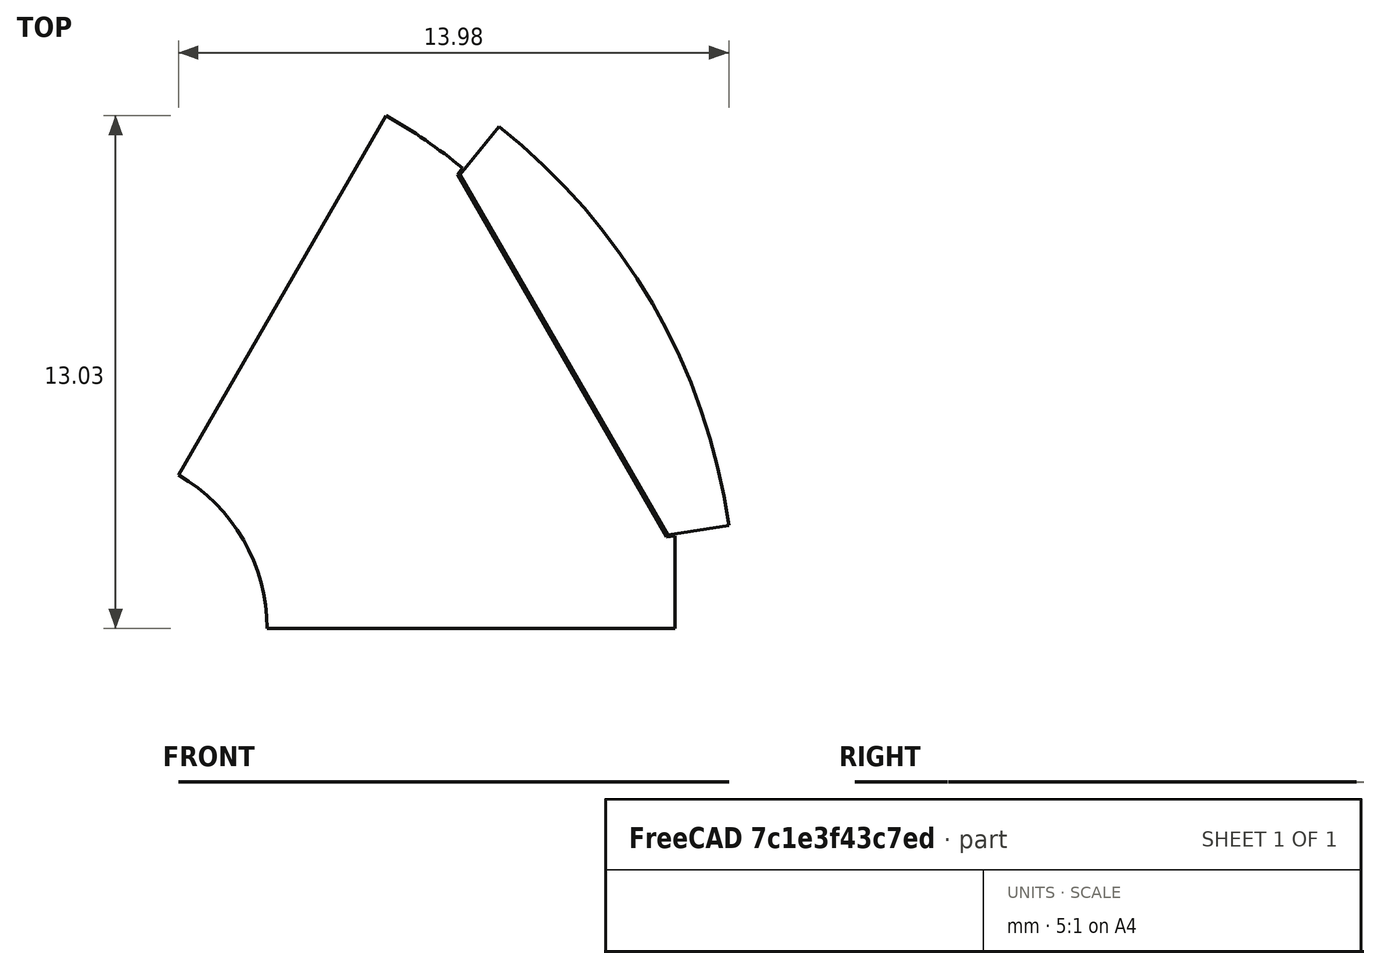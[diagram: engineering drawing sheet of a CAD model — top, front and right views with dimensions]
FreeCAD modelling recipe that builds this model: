
FCSTD DOCUMENT  (FreeCAD 0.18R4 (GitTag))
Label: rotor4
License: All rights reserved
LicenseURL: http://en.wikipedia.org/wiki/All_rights_reserved
objects: Sketcher::SketchObject×5, PartDesign::Body×2, Surface::Filling×2, Spreadsheet::Sheet×1
note: 9 computed .brp shape members not serialized (recipe doc carries the construction recipe); baked Part::Feature solids carry a one-line shape summary decoded from their .brp

FEATURE [Spreadsheet::Sheet] Spreadsheet  label="Variables"
  cells = A2=poleNumber; B2(poleNumber)=6; A3=outerDiameter; B3(outerDiameter)=33; D3=Calc Value; A4=innerDiameter; B4(innerDiameter)=9; D4=Input Value; A5=stackLength; B5(stackLength)=20; A6=stackingFactor; B6(stackingFactor)=0.95; A7=embrace; B7(embrace)=75; A8=contourRatio; B8(contourRatio)=80; A9=magnetAirgap; B9(magnetAirgap)=0.05; A10=poleSeparation; B10(poleSeparation)=2; A11=magnetWidth; B11(magnetWidth)=9; A12=magnetHeight; B12(magnetHeight)=2.8; A13=rib; B13(rib)=0.5; A14=bridgeCurved; B14(bridgeCurved)=0.5; A15=cutTop; B15(cutTop)=0.2; A16=cutBottom; B16(cutBottom)=0.25; A17=segmentAngle; B17(segmentAngle)==360 / poleNumber; A18=movePocketInwards; B18(movePocketInwards)=0.5; A19=cuttingThickness; B19(cuttingThickness)=0.1; A20=magnetLength; B20(magnetLength)==stackLength; A21=cut; B21(cut)=0.2; A22=ribShaft; B22(ribShaft)=0.5; A23=magnetEmbrace; B23(magnetEmbrace)=70; A24=magnetContourRatio; B24(magnetContourRatio)=95; A25=axialMisalignment; B25(axialMisalignment)=0.5
FEATURE [Sketcher::SketchObject] Sketch003  label="RotorSketch"
  MapMode = 5
  Support = -> [XY_Plane]
  expr: Constraints[32] = Variables.outerDiameter / 2 - Variables.magnetHeight - Variables.magnetAirgap + Spreadsheet.cutTop
  expr: Constraints[28] = Variables.segmentAngle * Variables.magnetEmbrace / 100
  expr: Constraints[15] = Variables.outerDiameter / 2
  expr: Constraints[14] = Variables.innerDiameter / 2
  expr: Constraints[50] = Spreadsheet.cut
  expr: Constraints[18] = Variables.segmentAngle / 2
  expr: Constraints[0] = Variables.segmentAngle
  expr: Constraints[23] = Variables.outerDiameter / 2 * Variables.magnetContourRatio / 100
  sketch-geometry (22):
    g0: LineSegment [constr] StartX=4.5 StartY=0 StartZ=0 EndX=16.5 EndY=0 EndZ=0
    g1: LineSegment [constr] StartX=2.25 StartY=3.89711 StartZ=0 EndX=8.25 EndY=14.2894 EndZ=0
    g2: LineSegment [constr] StartX=0 StartY=0 StartZ=0 EndX=4.5 EndY=0 EndZ=0
    g3: LineSegment [constr] StartX=0 StartY=0 StartZ=0 EndX=2.25 EndY=3.89711 EndZ=0
    g4: ArcOfCircle [constr] CenterX=0 CenterY=0 CenterZ=0 NormalX=0 NormalY=0 NormalZ=1 AngleXU=0 Radius=16.5 StartAngle=0 EndAngle=1.0472
    g5: ArcOfCircle CenterX=0 CenterY=0 CenterZ=0 NormalX=0 NormalY=0 NormalZ=1 AngleXU=0 Radius=4.5 StartAngle=0 EndAngle=1.0472
    g6: LineSegment [constr] StartX=0 StartY=0 StartZ=0 EndX=14.2894 EndY=8.25 EndZ=0
    g7: ArcOfCircle [constr] CenterX=0.714471 CenterY=0.4125 CenterZ=0 NormalX=0 NormalY=0 NormalZ=1 AngleXU=0 Radius=15.675 StartAngle=6.25687 EndAngle=7.3567
    g8: LineSegment [constr] StartX=0 StartY=0 StartZ=0 EndX=10.3838 EndY=12.8229 EndZ=0
    g9: LineSegment [constr] StartX=0 StartY=0 StartZ=0 EndX=16.2969 EndY=2.58117 EndZ=0
    g10: ArcOfCircle [constr] CenterX=0 CenterY=0 CenterZ=0 NormalX=0 NormalY=0 NormalZ=1 AngleXU=0 Radius=13.85 StartAngle=0 EndAngle=1.0472
    g11: LineSegment [constr] StartX=0 StartY=0 StartZ=0 EndX=9.33619 EndY=11.5292 EndZ=0
    g12: LineSegment [constr] StartX=0 StartY=0 StartZ=0 EndX=14.6527 EndY=2.32076 EndZ=0
    g13: LineSegment StartX=9.33619 StartY=11.5292 StartZ=0 EndX=14.6527 EndY=2.32076 EndZ=0
    g14: ArcOfCircle CenterX=0 CenterY=0 CenterZ=0 NormalX=0 NormalY=0 NormalZ=1 AngleXU=0 Radius=15.0496 StartAngle=0.890118 EndAngle=1.0472
    g15: LineSegment StartX=9.47101 StartY=11.6957 StartZ=0 EndX=9.33619 EndY=11.5292 EndZ=0
    g16: LineSegment [constr] StartX=9.33619 StartY=11.5292 StartZ=0 EndX=9.5094 EndY=11.6292 EndZ=0
    g17: LineSegment [constr] StartX=9.5094 StartY=11.6292 StartZ=0 EndX=9.47101 EndY=11.6957 EndZ=0
    g18: LineSegment StartX=14.6527 StartY=2.32076 StartZ=0 EndX=14.8643 EndY=2.35427 EndZ=0
    g19: LineSegment StartX=14.8643 StartY=2.35427 StartZ=0 EndX=14.8643 EndY=0 EndZ=0
    g20: LineSegment StartX=2.25 StartY=3.89711 StartZ=0 EndX=7.52479 EndY=13.0333 EndZ=0
    g21: LineSegment StartX=4.5 StartY=0 StartZ=0 EndX=14.8643 EndY=0 EndZ=0
  constraints (62):
    c: Angle(g0,g1) = 1.0472
    c: Coincident(g2,g-1)
    c: Coincident(g2,g0)
    c: Coincident(g3,g2)
    c: Coincident(g3,g1)
    c: Parallel(g2,g0)
    c: Parallel(g3,g1)
    c: Coincident(g4,g-1)
    c: Coincident(g4,g0)
    c: Coincident(g4,g1)
    c: Coincident(g5,g4)
    c: Coincident(g5,g1)
    c: Coincident(g5,g0)
    c: Angle(g-1,g2) = 0
    c: Radius(g5) = 4.5
    c: Radius(g4) = 16.5
    c: Coincident(g6,g5)
    c: PointOnObject(g6,g4)
    c: Angle(g-1,g6) = 0.523599
    c: PointOnObject(g7,g1)
    c: PointOnObject(g7,g0)
    c: PointOnObject(g6,g7)
    c: PointOnObject(g7,g6)
    c: Radius(g7) = 15.675
    c: Coincident(g8,g5)
    c: PointOnObject(g8,g4)
    c: Coincident(g9,g5)
    c: Symmetric(g8,g9,g6)
    c: Angle(g9,g8) = 0.733038
    c: Coincident(g10,g5)
    c: PointOnObject(g10,g1)
    c: PointOnObject(g10,g0)
    c: Radius(g10) = 13.85
    c: Coincident(g11,g5)
    c: PointOnObject(g11,g8)
    c: Coincident(g12,g5)
    c: PointOnObject(g12,g9)
    c: Equal(g11,g12)
    c: Coincident(g13,g11)
    c: Coincident(g13,g12)
    c: Tangent(g13,g10)
    c: Coincident(g14,g5)
    c: PointOnObject(g14,g8)
    c: Coincident(g15,g14)
    c: Coincident(g15,g13)
    c: Coincident(g16,g13)
    c: Coincident(g17,g16)
    c: Coincident(g17,g14)
    c: Angle(g17,g16) = 1.5708
    c: Angle(g13,g16) = 1.5708
    c: Distance(g16) = 0.2
    c: PointOnObject(g14,g1)
    c: Coincident(g18,g13)
    c: PointOnObject(g18,g9)
    c: Coincident(g19,g18)
    c: PointOnObject(g19,g0)
    c: Vertical(g19)
    c: Equal(g18,g15)
    c: Coincident(g20,g5)
    c: Coincident(g20,g14)
    c: Coincident(g21,g5)
    c: Coincident(g21,g19)
FEATURE [Sketcher::SketchObject] Sketch004  label="BoundingBox"
  MapMode = 5
  Support = -> [XY_Plane]
  expr: Constraints[8] = Variables.outerDiameter
  sketch-geometry (6):
    g0: LineSegment StartX=-16.5 StartY=-16.5 StartZ=0 EndX=16.5 EndY=-16.5 EndZ=0
    g1: LineSegment StartX=16.5 StartY=-16.5 StartZ=0 EndX=16.5 EndY=16.5 EndZ=0
    g2: LineSegment StartX=16.5 StartY=16.5 StartZ=0 EndX=-16.5 EndY=16.5 EndZ=0
    g3: LineSegment StartX=-16.5 StartY=16.5 StartZ=0 EndX=-16.5 EndY=-16.5 EndZ=0
    g4: LineSegment [constr] StartX=-16.5 StartY=-16.5 StartZ=0 EndX=16.5 EndY=16.5 EndZ=0
    g5: GeomPoint X=0 Y=0 Z=0
  constraints (14):
    c: Coincident(g0,g1)
    c: Coincident(g1,g2)
    c: Coincident(g2,g3)
    c: Coincident(g3,g0)
    c: Horizontal(g0)
    c: Horizontal(g2)
    c: Vertical(g1)
    c: Vertical(g3)
    c: DistanceY(g1,g1) = 33
    c: Equal(g2,g1)
    c: Coincident(g4,g0)
    c: Coincident(g4,g1)
    c: Symmetric(g0,g1,g5)
    c: Coincident(g-1,g5)
FEATURE [Sketcher::SketchObject] Sketch005  label="RotorSideSketch"
  MapMode = 5
  Support = -> [XY_Plane001]
  expr: Constraints[22] = Variables.stackLength / 2 - Variables.axialMisalignment
  expr: Constraints[9] = Variables.outerDiameter / 2
  expr: Constraints[8] = Variables.innerDiameter / 2
  expr: Constraints[7] = Variables.stackLength
  sketch-geometry (8):
    g0: LineSegment StartX=-9.5 StartY=4.5 StartZ=0 EndX=10.5 EndY=4.5 EndZ=0
    g1: LineSegment StartX=10.5 StartY=4.5 StartZ=0 EndX=10.5 EndY=16.5 EndZ=0
    g2: LineSegment StartX=10.5 StartY=16.5 StartZ=0 EndX=-9.5 EndY=16.5 EndZ=0
    g3: LineSegment StartX=-9.5 StartY=16.5 StartZ=0 EndX=-9.5 EndY=4.5 EndZ=0
    g4: LineSegment StartX=-9.5 StartY=-4.5 StartZ=0 EndX=10.5 EndY=-4.5 EndZ=0
    g5: LineSegment StartX=10.5 StartY=-4.5 StartZ=0 EndX=10.5 EndY=-16.5 EndZ=0
    g6: LineSegment StartX=10.5 StartY=-16.5 StartZ=0 EndX=-9.5 EndY=-16.5 EndZ=0
    g7: LineSegment StartX=-9.5 StartY=-16.5 StartZ=0 EndX=-9.5 EndY=-4.5 EndZ=0
  constraints (23):
    c: Coincident(g0,g1)
    c: Coincident(g1,g2)
    c: Coincident(g2,g3)
    c: Coincident(g3,g0)
    c: Horizontal(g0)
    c: Vertical(g1)
    c: Vertical(g3)
    c: DistanceX(g2,g2) = 20
    c: DistanceY(g-1,g0) = 4.5
    c: DistanceY(g-1,g1) = 16.5
    c: Coincident(g4,g5)
    c: Coincident(g5,g6)
    c: Coincident(g6,g7)
    c: Coincident(g7,g4)
    c: Horizontal(g4)
    c: Vertical(g5)
    c: Vertical(g7)
    c: Equal(g4,g0)
    c: Equal(g7,g3)
    c: Horizontal(g6)
    c: Horizontal(g2)
    c: Symmetric(g0,g4,g-1)
    c: DistanceX(g0,g-1) = 9.5
FEATURE [Sketcher::SketchObject] Sketch006  label="MagnetSideSketch"
  ExternalGeometry = -> [Sketch005]
  MapMode = 5
  Support = -> [XY_Plane001]
  expr: Constraints[20] = Variables.stackLength / 2 - Variables.axialMisalignment
  expr: Constraints[7] = Variables.magnetHeight
  sketch-geometry (8):
    g0: LineSegment StartX=-9.5 StartY=13.7 StartZ=0 EndX=10.5 EndY=13.7 EndZ=0
    g1: LineSegment StartX=10.5 StartY=13.7 StartZ=0 EndX=10.5 EndY=16.5 EndZ=0
    g2: LineSegment StartX=10.5 StartY=16.5 StartZ=0 EndX=-9.5 EndY=16.5 EndZ=0
    g3: LineSegment StartX=-9.5 StartY=16.5 StartZ=0 EndX=-9.5 EndY=13.7 EndZ=0
    g4: LineSegment StartX=-9.5 StartY=-16.5 StartZ=0 EndX=10.5 EndY=-16.5 EndZ=0
    g5: LineSegment StartX=10.5 StartY=-16.5 StartZ=0 EndX=10.5 EndY=-13.7 EndZ=0
    g6: LineSegment StartX=10.5 StartY=-13.7 StartZ=0 EndX=-9.5 EndY=-13.7 EndZ=0
    g7: LineSegment StartX=-9.5 StartY=-13.7 StartZ=0 EndX=-9.5 EndY=-16.5 EndZ=0
  constraints (21):
    c: Coincident(g0,g1)
    c: Coincident(g1,g2)
    c: Coincident(g2,g3)
    c: Coincident(g3,g0)
    c: Horizontal(g0)
    c: Vertical(g1)
    c: Vertical(g3)
    c: DistanceY(g1,g1) = 2.8
    c: Coincident(g4,g5)
    c: Coincident(g5,g6)
    c: Coincident(g6,g7)
    c: Coincident(g7,g4)
    c: Horizontal(g4)
    c: Vertical(g5)
    c: Vertical(g7)
    c: Symmetric(g6,g0,g-1)
    c: Symmetric(g5,g0,g-1)
    c: Equal(g7,g3)
    c: Coincident(g1,g-3)
    c: Horizontal(g2)
    c: DistanceX(g0,g-1) = 9.5
FEATURE [PartDesign::Body] Body001  label="SideView"
  Group = -> [Sketch005,Sketch006]
  Origin = -> Origin001
FEATURE [Surface::Filling] Surface  label="Rotor_Surface"
  Anisotropy = false
  BoundaryEdges = -> [Sketch003]
  BoundaryOrder = [0,0,0,0,0,0,0,0]
  Degree = 3
  Iterations = 2
  MaximumDegree = 8
  MaximumSegments = 9
  PointsOnCurve = 15
  TolAngular = 0.01
  TolCurvature = 0.1
  Tolerance2d = 1e-05
  Tolerance3d = 0.0001
FEATURE [Sketcher::SketchObject] Sketch007  label="MagnetSketch"
  MapMode = 5
  Support = -> [XY_Plane]
  expr: Constraints[80] = Variables.magnetAirgap
  expr: Constraints[65] = Variables.magnetAirgap
  expr: Constraints[30] = Variables.outerDiameter / 2 - Variables.magnetHeight - Variables.magnetAirgap + Spreadsheet.cutTop
  expr: Constraints[21] = Variables.outerDiameter / 2 * Variables.magnetContourRatio / 100
  expr: Constraints[26] = Variables.segmentAngle * Variables.magnetEmbrace / 100
  expr: Constraints[14] = Variables.innerDiameter / 2
  expr: Constraints[71] = Variables.magnetAirgap
  expr: Constraints[15] = Variables.outerDiameter / 2
  expr: Constraints[48] = Spreadsheet.cut
  expr: Constraints[18] = Variables.segmentAngle / 2
  expr: Constraints[0] = Variables.segmentAngle
  sketch-geometry (30):
    g0: LineSegment [constr] StartX=4.5 StartY=0 StartZ=0 EndX=16.5 EndY=0 EndZ=0
    g1: LineSegment [constr] StartX=2.25 StartY=3.89711 StartZ=0 EndX=8.25 EndY=14.2894 EndZ=0
    g2: LineSegment [constr] StartX=0 StartY=0 StartZ=0 EndX=4.5 EndY=0 EndZ=0
    g3: LineSegment [constr] StartX=0 StartY=0 StartZ=0 EndX=2.25 EndY=3.89711 EndZ=0
    g4: ArcOfCircle [constr] CenterX=0 CenterY=0 CenterZ=0 NormalX=0 NormalY=0 NormalZ=1 AngleXU=0 Radius=16.5 StartAngle=0 EndAngle=1.0472
    g5: ArcOfCircle [constr] CenterX=0 CenterY=0 CenterZ=0 NormalX=0 NormalY=0 NormalZ=1 AngleXU=0 Radius=4.5 StartAngle=0 EndAngle=1.0472
    g6: LineSegment [constr] StartX=0 StartY=0 StartZ=0 EndX=14.2894 EndY=8.25 EndZ=0
    g7: ArcOfCircle CenterX=0.714471 CenterY=0.4125 CenterZ=0 NormalX=0 NormalY=0 NormalZ=1 AngleXU=0 Radius=15.675 StartAngle=0.141402 EndAngle=0.905796
    g8: LineSegment [constr] StartX=0 StartY=0 StartZ=0 EndX=10.3838 EndY=12.8229 EndZ=0
    g9: LineSegment [constr] StartX=0 StartY=0 StartZ=0 EndX=16.2969 EndY=2.58117 EndZ=0
    g10: ArcOfCircle [constr] CenterX=0 CenterY=0 CenterZ=0 NormalX=0 NormalY=0 NormalZ=1 AngleXU=0 Radius=13.85 StartAngle=0 EndAngle=1.0472
    g11: LineSegment [constr] StartX=0 StartY=0 StartZ=0 EndX=9.33619 EndY=11.5292 EndZ=0
    g12: LineSegment [constr] StartX=0 StartY=0 StartZ=0 EndX=14.6527 EndY=2.32076 EndZ=0
    g13: LineSegment [constr] StartX=9.33619 StartY=11.5292 StartZ=0 EndX=14.6527 EndY=2.32076 EndZ=0
    g14: ArcOfCircle [constr] CenterX=0 CenterY=0 CenterZ=0 NormalX=0 NormalY=0 NormalZ=1 AngleXU=0 Radius=15.0496 StartAngle=0.890118 EndAngle=1.0472
    g15: LineSegment [constr] StartX=9.47101 StartY=11.6957 StartZ=0 EndX=9.33619 EndY=11.5292 EndZ=0
    g16: LineSegment [constr] StartX=9.33619 StartY=11.5292 StartZ=0 EndX=9.5094 EndY=11.6292 EndZ=0
    g17: LineSegment [constr] StartX=9.5094 StartY=11.6292 StartZ=0 EndX=9.47101 EndY=11.6957 EndZ=0
    g18: LineSegment [constr] StartX=14.6527 StartY=2.32076 StartZ=0 EndX=14.8643 EndY=2.35427 EndZ=0
    g19: LineSegment [constr] StartX=14.8643 StartY=2.35427 StartZ=0 EndX=14.8643 EndY=0 EndZ=0
    g20: LineSegment [constr] StartX=2.25 StartY=3.89711 StartZ=0 EndX=7.52479 EndY=13.0333 EndZ=0
    g21: LineSegment [constr] StartX=4.5 StartY=0 StartZ=0 EndX=14.8643 EndY=0 EndZ=0
    g22: LineSegment [constr] StartX=10.4226 StartY=12.7914 StartZ=0 EndX=8.75178 EndY=10.7345 EndZ=0
    g23: LineSegment [constr] StartX=10.3838 StartY=12.8229 StartZ=0 EndX=10.4226 EndY=12.7914 EndZ=0
    g24: LineSegment [constr] StartX=13.6722 StartY=2.21202 StartZ=0 EndX=16.289 EndY=2.63054 EndZ=0
    g25: LineSegment [constr] StartX=16.289 StartY=2.63054 StartZ=0 EndX=16.2969 EndY=2.58117 EndZ=0
    g26: LineSegment StartX=9.39535 StartY=11.5268 StartZ=0 EndX=14.6802 EndY=2.37323 EndZ=0
    g27: LineSegment [constr] StartX=9.39535 StartY=11.5268 StartZ=0 EndX=9.35205 EndY=11.5018 EndZ=0
    g28: LineSegment StartX=9.39535 StartY=11.5268 StartZ=0 EndX=10.3869 EndY=12.7474 EndZ=0
    g29: LineSegment StartX=14.6802 StartY=2.37323 StartZ=0 EndX=16.233 EndY=2.62159 EndZ=0
  constraints (85):
    c: Angle(g0,g1) = 1.0472
    c: Coincident(g2,g-1)
    c: Coincident(g2,g0)
    c: Coincident(g3,g2)
    c: Coincident(g3,g1)
    c: Parallel(g2,g0)
    c: Parallel(g3,g1)
    c: Coincident(g4,g-1)
    c: Coincident(g4,g0)
    c: Coincident(g4,g1)
    c: Coincident(g5,g4)
    c: Coincident(g5,g1)
    c: Coincident(g5,g0)
    c: Angle(g-1,g2) = 0
    c: Radius(g5) = 4.5
    c: Radius(g4) = 16.5
    c: Coincident(g6,g5)
    c: PointOnObject(g6,g4)
    c: Angle(g-1,g6) = 0.523599
    c: PointOnObject(g6,g7)
    c: PointOnObject(g7,g6)
    c: Radius(g7) = 15.675
    c: Coincident(g8,g5)
    c: PointOnObject(g8,g4)
    c: Coincident(g9,g5)
    c: Symmetric(g8,g9,g6)
    c: Angle(g9,g8) = 0.733038
    c: Coincident(g10,g5)
    c: PointOnObject(g10,g1)
    c: PointOnObject(g10,g0)
    c: Radius(g10) = 13.85
    c: Coincident(g11,g5)
    c: PointOnObject(g11,g8)
    c: Coincident(g12,g5)
    c: PointOnObject(g12,g9)
    c: Equal(g11,g12)
    c: Coincident(g13,g11)
    c: Coincident(g13,g12)
    c: Tangent(g13,g10)
    c: Coincident(g14,g5)
    c: PointOnObject(g14,g8)
    c: Coincident(g15,g14)
    c: Coincident(g15,g13)
    c: Coincident(g16,g13)
    c: Coincident(g17,g16)
    c: Coincident(g17,g14)
    c: Angle(g17,g16) = 1.5708
    c: Angle(g13,g16) = 1.5708
    c: Distance(g16) = 0.2
    c: PointOnObject(g14,g1)
    c: Coincident(g18,g13)
    c: PointOnObject(g18,g9)
    c: Coincident(g19,g18)
    c: PointOnObject(g19,g0)
    c: Vertical(g19)
    c: Equal(g18,g15)
    c: Coincident(g20,g5)
    c: Coincident(g20,g14)
    c: Coincident(g21,g5)
    c: Coincident(g21,g19)
    c: PointOnObject(g22,g4)
    c: PointOnObject(g22,g10)
    c: Coincident(g23,g8)
    c: Coincident(g23,g22)
    c: Angle(g23,g22) = 1.5708
    c: Distance(g23) = 0.05
    c: PointOnObject(g24,g10)
    c: PointOnObject(g24,g4)
    c: Coincident(g25,g24)
    c: Coincident(g25,g9)
    c: Angle(g24,g25) = 1.5708
    c: Distance(g25) = 0.05
    c: PointOnObject(g7,g24)
    c: PointOnObject(g7,g22)
    c: PointOnObject(g26,g24)
    c: Parallel(g26,g13)
    c: Coincident(g27,g26)
    c: PointOnObject(g27,g13)
    c: PointOnObject(g26,g22)
    c: Angle(g27,g26) = 1.5708
    c: Distance(g27) = 0.05
    c: Coincident(g28,g26)
    c: Coincident(g28,g7)
    c: Coincident(g29,g26)
    c: Coincident(g29,g7)
FEATURE [PartDesign::Body] Body  label="TopView"
  Group = -> [Sketch003,Sketch004,Sketch007]
  Origin = -> Origin
FEATURE [Surface::Filling] Surface001  label="Magnet_Surface"
  Anisotropy = false
  BoundaryEdges = -> [Sketch007]
  BoundaryOrder = [0,0,0,0]
  Degree = 3
  Iterations = 2
  MaximumDegree = 8
  MaximumSegments = 9
  PointsOnCurve = 15
  TolAngular = 0.01
  TolCurvature = 0.1
  Tolerance2d = 1e-05
  Tolerance3d = 0.0001
